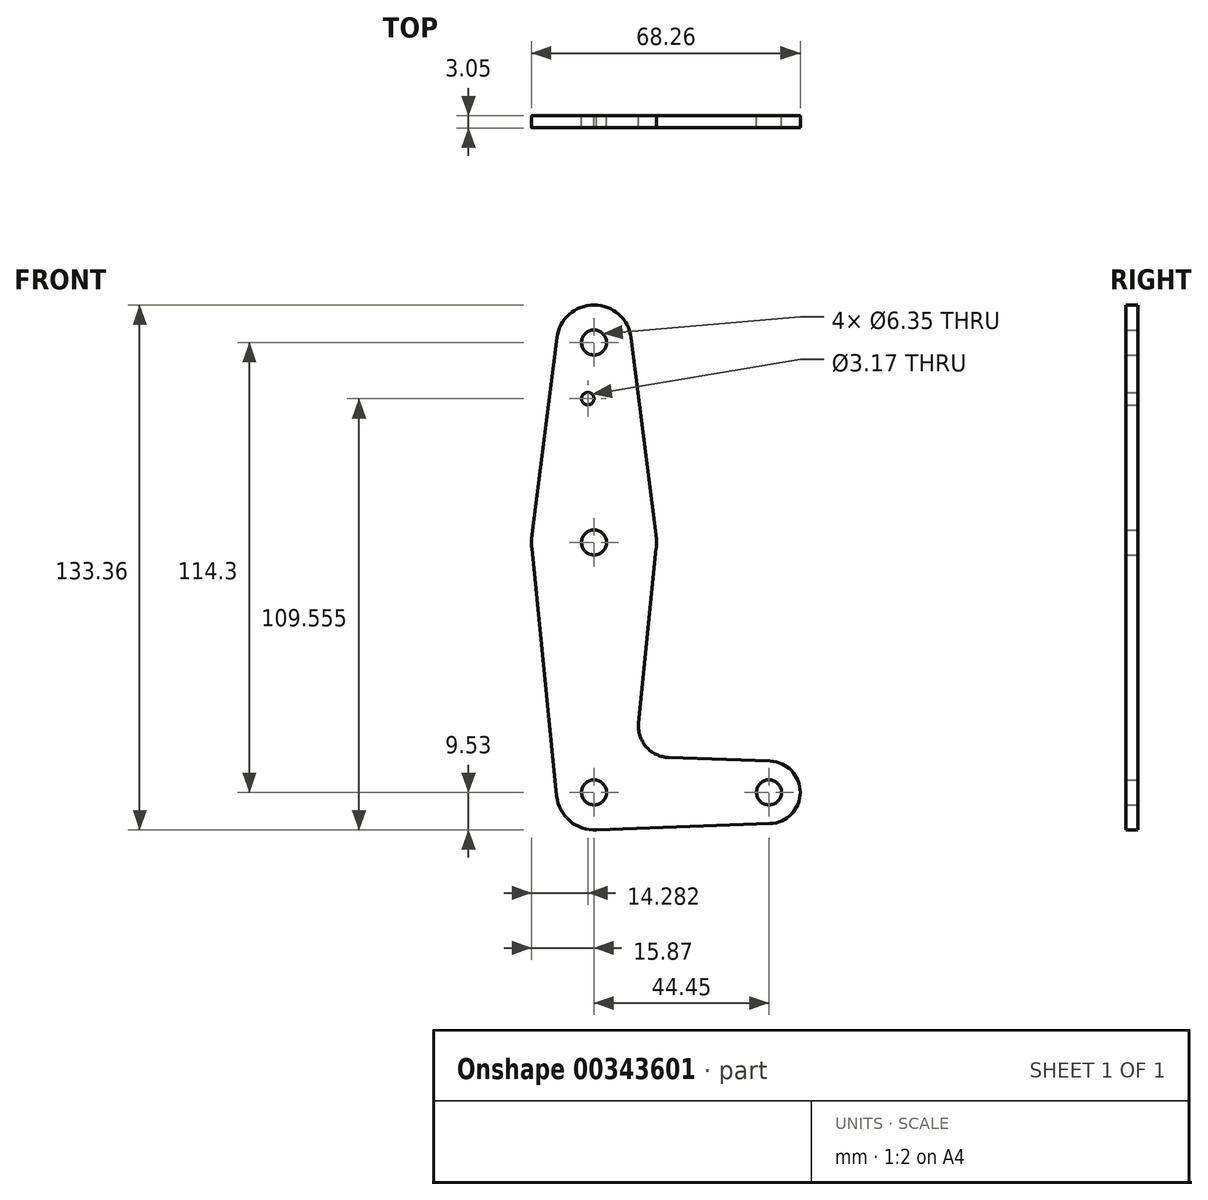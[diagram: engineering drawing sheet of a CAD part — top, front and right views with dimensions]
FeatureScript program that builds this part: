
annotation { "Feature Type Name" : "Feature", "Feature Type Description" : "" }
export const myFeature = defineFeature(function(context is Context, id is Id, definition is map)
    precondition{}
    {
        {
            var Q0;
            Q0=qCreatedBy(makeId("Front.planeOp"),FACE);
            var sketch = newSketch(context, id + "F0", { "sketchPlane" : qUnion([Q0])});
            skLineSegment(sketch, "E0", {"start": v(0, 0) * mm, "end": v(0, 114.3) * mm, "construction": true});
            skLineSegment(sketch, "E1", {"start": v(0, 0) * mm, "end": v(44.45, 0) * mm, "construction": true});
            skCircle(sketch, "E2", {"center": v(0, 0) * mm, "radius": 9.53 * mm});
            skCircle(sketch, "E3", {"center": v(0, 63.5) * mm, "radius": 15.88 * mm});
            skCircle(sketch, "E4", {"center": v(0, 114.3) * mm, "radius": 9.53 * mm});
            skCircle(sketch, "E5", {"center": v(44.45, 0) * mm, "radius": 7.94 * mm});
            skLineSegment(sketch, "E6", {"start": v(-9.57, 0) * mm, "end": v(9.52, 0) * mm, "construction": true});
            skLineSegment(sketch, "E7", {"start": v(18.97, 8.85) * mm, "end": v(44.73, 7.93) * mm});
            skLineSegment(sketch, "E8", {"start": v(0, -9.53) * mm, "end": v(44.73, -7.93) * mm});
            skLineSegment(sketch, "E9", {"start": v(-9.48, -0.95) * mm, "end": v(-15.8, 61.91) * mm});
            skLineSegment(sketch, "E10", {"start": v(-15.75, 65.48) * mm, "end": v(-9.45, 115.5) * mm});
            skCircle(sketch, "E11", {"center": v(0, 114.3) * mm, "radius": 3.18 * mm});
            skCircle(sketch, "E12", {"center": v(0, 63.5) * mm, "radius": 3.18 * mm});
            skCircle(sketch, "E13", {"center": v(0, 0) * mm, "radius": 3.18 * mm});
            skCircle(sketch, "E14", {"center": v(44.45, 0) * mm, "radius": 3.18 * mm});
            skCircle(sketch, "E15", {"center": v(-1.59, 100.03) * mm, "radius": 1.59 * mm});
            skLineSegment(sketch, "E16", {"start": v(15.8, 61.91) * mm, "end": v(11.34, 17.59) * mm});
            skLineSegment(sketch, "E17", {"start": v(15.75, 65.48) * mm, "end": v(9.45, 115.5) * mm});
            skArc(sketch, "E18.filletArc", {"start": v(11.34, 17.59) * mm, "mid": v(13.26, 11.57) * mm, "end": v(18.97, 8.85) * mm});
            skSolve(sketch);
        }
        {
            var Q0;
            Q0 = qSketchRegion(id + "F0", true);
            extrude(context, id + "F1", {"entities" : qUnion([Q0]), "depth" : 3.05 * mm});
        }
    });
